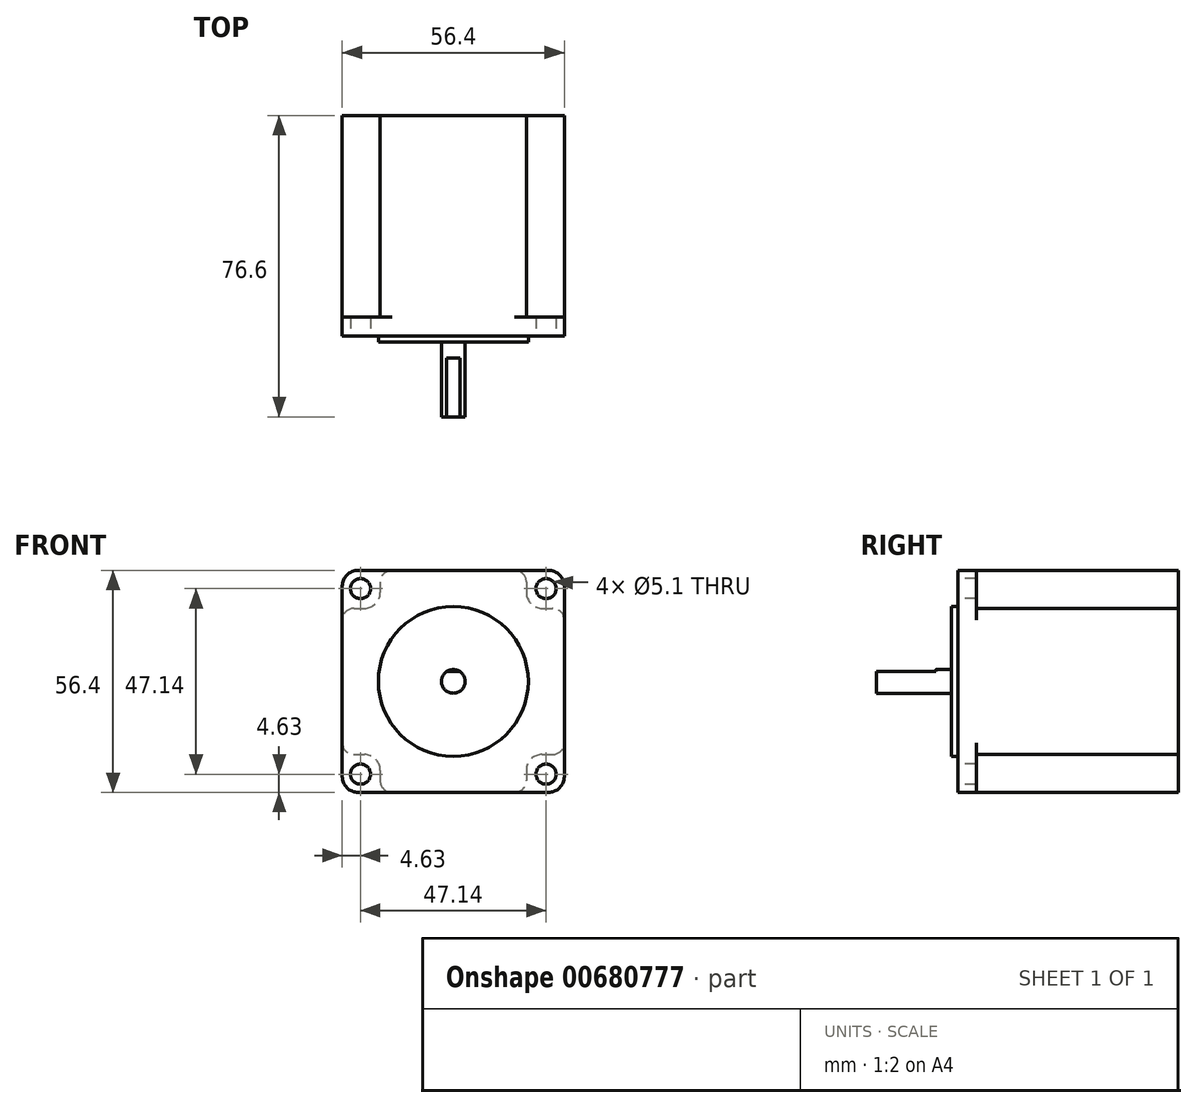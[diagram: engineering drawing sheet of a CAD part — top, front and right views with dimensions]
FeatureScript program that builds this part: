
annotation { "Feature Type Name" : "Feature", "Feature Type Description" : "" }
export const myFeature = defineFeature(function(context is Context, id is Id, definition is map)
    precondition{}
    {
        {
            var Q0;
            Q0=qCreatedBy(makeId("Front.planeOp"),FACE);
            var sketch = newSketch(context, id + "F0", { "sketchPlane" : qUnion([Q0])});
            skLineSegment(sketch, "E0.rect.bottom", {"start": v(-28.2, 28.2) * mm, "end": v(28.2, 28.2) * mm});
            skLineSegment(sketch, "E0.rect.top", {"start": v(-28.2, -28.2) * mm, "end": v(28.2, -28.2) * mm});
            skLineSegment(sketch, "E0.rect.left", {"start": v(-28.2, 28.2) * mm, "end": v(-28.2, -28.2) * mm});
            skLineSegment(sketch, "E0.rect.right", {"start": v(28.2, 28.2) * mm, "end": v(28.2, -28.2) * mm});
            skPoint(sketch, "E0.rect.middle", {"position": v(0, 0) * mm});
            skCircle(sketch, "E1", {"center": v(0, 0) * mm, "radius": 19.05 * mm});
            skCircle(sketch, "E2", {"center": v(0, 0) * mm, "radius": 3 * mm});
            skCircle(sketch, "E3", {"center": v(-23.57, 23.57) * mm, "radius": 2.55 * mm});
            skCircle(sketch, "E4", {"center": v(23.57, 23.57) * mm, "radius": 2.55 * mm});
            skCircle(sketch, "E5", {"center": v(23.57, -23.57) * mm, "radius": 2.55 * mm});
            skCircle(sketch, "E6", {"center": v(-23.57, -23.57) * mm, "radius": 2.55 * mm});
            skLineSegment(sketch, "E7.rect.bottom", {"start": v(-23.57, 23.57) * mm, "end": v(23.57, 23.57) * mm, "construction": true});
            skLineSegment(sketch, "E7.rect.top", {"start": v(-23.57, -23.57) * mm, "end": v(23.57, -23.57) * mm, "construction": true});
            skLineSegment(sketch, "E7.rect.left", {"start": v(-23.57, 23.57) * mm, "end": v(-23.57, -23.57) * mm, "construction": true});
            skLineSegment(sketch, "E7.rect.right", {"start": v(23.57, 23.57) * mm, "end": v(23.57, -23.57) * mm, "construction": true});
            skSolve(sketch);
        }
        {
            var Q0;
            Q0=makeQuery(id+"F0.imprint","IMPRINT",FACE,{"disambiguationData":[TD([[makeQuery(id+"F0.imprint","IMPRINT",EDGE,{"derivedFrom":sQuery(id+"F0.wireOp",EDGE,"E0.rect.bottom")}),-1.0]])]});
            var Q1;
            Q1=makeQuery(id+"F0.imprint","IMPRINT",FACE,{"disambiguationData":[TD([[makeQuery(id+"F0.imprint","IMPRINT",EDGE,{"derivedFrom":sQuery(id+"F0.wireOp",EDGE,"E1")}),1.0]])]});
            var Q2;
            Q2=makeQuery(id+"F0.imprint","IMPRINT",FACE,{"disambiguationData":[TD([[makeQuery(id+"F0.imprint","IMPRINT",EDGE,{"derivedFrom":sQuery(id+"F0.wireOp",EDGE,"E2")}),1.0]])]});
            extrude(context, id + "F1", {"entities" : qUnion([Q0, Q1, Q2]), "oppositeDirection" : true, "depth" : 4.8 * mm});
        }
        {
            var Q0;
            Q0=makeQuery(id+"F0.imprint","IMPRINT",FACE,{"disambiguationData":[TD([[makeQuery(id+"F0.imprint","IMPRINT",EDGE,{"derivedFrom":sQuery(id+"F0.wireOp",EDGE,"E1")}),1.0]])]});
            extrude(context, id + "F2", {"entities" : qUnion([Q0]), "depth" : 1.6 * mm, "offsetDistance" : 25 * mm});
        }
        {
            var Q0;
            Q0=makeQuery(id+"F0.imprint","IMPRINT",FACE,{"disambiguationData":[TD([[makeQuery(id+"F0.imprint","IMPRINT",EDGE,{"derivedFrom":sQuery(id+"F0.wireOp",EDGE,"E2")}),1.0]])]});
            extrude(context, id + "F3", {"entities" : qUnion([Q0]), "depth" : 20.6 * mm, "offsetDistance" : 25 * mm});
        }
        {
            var Q0;
            Q0=makeQuery(id+"F1.opExtrude","SWEPT_EDGE",EDGE,{"disambiguationData":[OSD([sQuery(id+"F0.wireOp",EDGE,"E0.rect.bottom"),sQuery(id+"F0.wireOp",EDGE,"E0.rect.left")])]});
            var Q1;
            Q1=makeQuery(id+"F1.opExtrude","SWEPT_EDGE",EDGE,{"disambiguationData":[OSD([sQuery(id+"F0.wireOp",EDGE,"E0.rect.bottom"),sQuery(id+"F0.wireOp",EDGE,"E0.rect.right")])]});
            var Q2;
            Q2=makeQuery(id+"F1.opExtrude","SWEPT_EDGE",EDGE,{"disambiguationData":[OSD([sQuery(id+"F0.wireOp",EDGE,"E0.rect.top"),sQuery(id+"F0.wireOp",EDGE,"E0.rect.right")])]});
            var Q3;
            Q3=makeQuery(id+"F1.opExtrude","SWEPT_EDGE",EDGE,{"disambiguationData":[OSD([sQuery(id+"F0.wireOp",EDGE,"E0.rect.top"),sQuery(id+"F0.wireOp",EDGE,"E0.rect.left")])]});
            fillet(context, id + "F4", {"entities" : qUnion([Q0, Q1, Q2, Q3]), "radius" : 4 * mm, "tangentPropagation" : true, "allowEdgeOverflow" : false});
        }
        {
            var Q0;
            Q0=makeQuery(id+"F1.opExtrude","SWEPT_FACE",FACE,{"disambiguationData":[OSD([sQuery(id+"F0.wireOp",EDGE,"E0.rect.left")])]});
            var sketch = newSketch(context, id + "F5", { "sketchPlane" : qUnion([Q0])});
            skLineSegment(sketch, "E8", {"start": v(1.6, 3) * mm, "end": v(20.6, 3) * mm});
            skLineSegment(sketch, "E9.0", {"start": v(20.6, 3) * mm, "end": v(20.6, -3) * mm});
            skLineSegment(sketch, "E10", {"start": v(5.6, 3) * mm, "end": v(5.6, 2.5) * mm});
            skLineSegment(sketch, "E11", {"start": v(5.6, 2.5) * mm, "end": v(20.6, 2.5) * mm});
            skSolve(sketch);
        }
        {
            var Q0;
            {var subQ1=sQuery(id+"F5.wireOp",EDGE,"E10");Q0=makeQuery(id+"F5.imprint","IMPRINT",FACE,{"disambiguationData":[TD([[makeQuery(id+"F5.imprint","IMPRINT",EDGE,{"derivedFrom":subQ1}),1.0]])]});}
            extrude(context, id + "F6", {"entities" : qUnion([Q0]), "operationType" : NewBodyOperationType.REMOVE, "endBound" : BoundingType.THROUGH_ALL, "oppositeDirection" : true, "depth" : 25 * mm});
        }
        {
            var Q0;
            Q0=qCreatedBy(makeId("Front.planeOp"),FACE);
            var sketch = newSketch(context, id + "F7", { "sketchPlane" : qUnion([Q0])});
            skPoint(sketch, "E12.rect.middle", {"position": v(0, 0.02) * mm});
            skPoint(sketch, "E13", {"position": v(0, 0) * mm});
            skLineSegment(sketch, "E14.rect.bottom", {"start": v(-18.57, 28.2) * mm, "end": v(18.57, 28.2) * mm});
            skLineSegment(sketch, "E14.rect.top", {"start": v(-18.57, -28.2) * mm, "end": v(18.57, -28.2) * mm});
            skLineSegment(sketch, "E14.rect.left", {"start": v(-18.57, 28.2) * mm, "end": v(-18.57, -28.2) * mm});
            skLineSegment(sketch, "E14.rect.right", {"start": v(18.57, 28.2) * mm, "end": v(18.57, -28.2) * mm});
            skLineSegment(sketch, "E15.rect.bottom", {"start": v(-28.2, 18.57) * mm, "end": v(28.2, 18.57) * mm});
            skLineSegment(sketch, "E15.rect.top", {"start": v(-28.2, -18.57) * mm, "end": v(28.2, -18.57) * mm});
            skLineSegment(sketch, "E15.rect.left", {"start": v(-28.2, 18.57) * mm, "end": v(-28.2, -18.57) * mm});
            skLineSegment(sketch, "E15.rect.right", {"start": v(28.2, 18.57) * mm, "end": v(28.2, -18.57) * mm});
            skSolve(sketch);
        }
        {
            var Q0;
            Q0=qSketchRegion(id+"F7",true);
            extrude(context, id + "F8", {"entities" : qUnion([Q0]), "operationType" : NewBodyOperationType.ADD, "oppositeDirection" : true, "depth" : 56 * mm});
        }
        {
            var Q0;
            Q0=makeQuery(id+"F8.opExtrude","SWEPT_EDGE",EDGE,{"disambiguationData":[OSD([sQuery(id+"F7.wireOp",EDGE,"E14.rect.right"),sQuery(id+"F7.wireOp",EDGE,"E15.rect.bottom")])]});
            var Q1;
            Q1=makeQuery(id+"F8.opExtrude","SWEPT_EDGE",EDGE,{"disambiguationData":[OSD([sQuery(id+"F7.wireOp",EDGE,"E14.rect.left"),sQuery(id+"F7.wireOp",EDGE,"E15.rect.bottom")])]});
            var Q2;
            Q2=makeQuery(id+"F8.opExtrude","SWEPT_EDGE",EDGE,{"disambiguationData":[OSD([sQuery(id+"F7.wireOp",EDGE,"E14.rect.left"),sQuery(id+"F7.wireOp",EDGE,"E15.rect.top")])]});
            var Q3;
            Q3=makeQuery(id+"F8.opExtrude","SWEPT_EDGE",EDGE,{"disambiguationData":[OSD([sQuery(id+"F7.wireOp",EDGE,"E14.rect.right"),sQuery(id+"F7.wireOp",EDGE,"E15.rect.top")])]});
            fillet(context, id + "F9", {"entities" : qUnion([Q0, Q1, Q2, Q3]), "radius" : 4 * mm, "tangentPropagation" : true, "allowEdgeOverflow" : false});
        }
        {
            var Q0;
            Q0=makeQuery(id+"F8.opExtrude","SWEPT_EDGE",EDGE,{"disambiguationData":[OSD([sQuery(id+"F7.wireOp",EDGE,"E14.rect.bottom"),sQuery(id+"F7.wireOp",EDGE,"E14.rect.right")])]});
            var Q1;
            Q1=makeQuery(id+"F8.opExtrude","SWEPT_EDGE",EDGE,{"disambiguationData":[OSD([sQuery(id+"F7.wireOp",EDGE,"E15.rect.bottom"),sQuery(id+"F7.wireOp",EDGE,"E15.rect.right")])]});
            var Q2;
            Q2=makeQuery(id+"F8.opExtrude","SWEPT_EDGE",EDGE,{"disambiguationData":[OSD([sQuery(id+"F7.wireOp",EDGE,"E15.rect.top"),sQuery(id+"F7.wireOp",EDGE,"E15.rect.right")])]});
            var Q3;
            Q3=makeQuery(id+"F8.opExtrude","SWEPT_EDGE",EDGE,{"disambiguationData":[OSD([sQuery(id+"F7.wireOp",EDGE,"E14.rect.top"),sQuery(id+"F7.wireOp",EDGE,"E14.rect.right")])]});
            var Q4;
            Q4=makeQuery(id+"F8.opExtrude","SWEPT_EDGE",EDGE,{"disambiguationData":[OSD([sQuery(id+"F7.wireOp",EDGE,"E14.rect.top"),sQuery(id+"F7.wireOp",EDGE,"E14.rect.left")])]});
            var Q5;
            Q5=makeQuery(id+"F8.opExtrude","SWEPT_EDGE",EDGE,{"disambiguationData":[OSD([sQuery(id+"F7.wireOp",EDGE,"E15.rect.top"),sQuery(id+"F7.wireOp",EDGE,"E15.rect.left")])]});
            var Q6;
            Q6=makeQuery(id+"F8.opExtrude","SWEPT_EDGE",EDGE,{"disambiguationData":[OSD([sQuery(id+"F7.wireOp",EDGE,"E15.rect.bottom"),sQuery(id+"F7.wireOp",EDGE,"E15.rect.left")])]});
            var Q7;
            Q7=makeQuery(id+"F8.opExtrude","SWEPT_EDGE",EDGE,{"disambiguationData":[OSD([sQuery(id+"F7.wireOp",EDGE,"E14.rect.bottom"),sQuery(id+"F7.wireOp",EDGE,"E14.rect.left")])]});
            fillet(context, id + "F10", {"entities" : qUnion([Q0, Q1, Q2, Q3, Q4, Q5, Q6, Q7]), "radius" : 3 * mm, "tangentPropagation" : true, "allowEdgeOverflow" : false});
        }
    });
